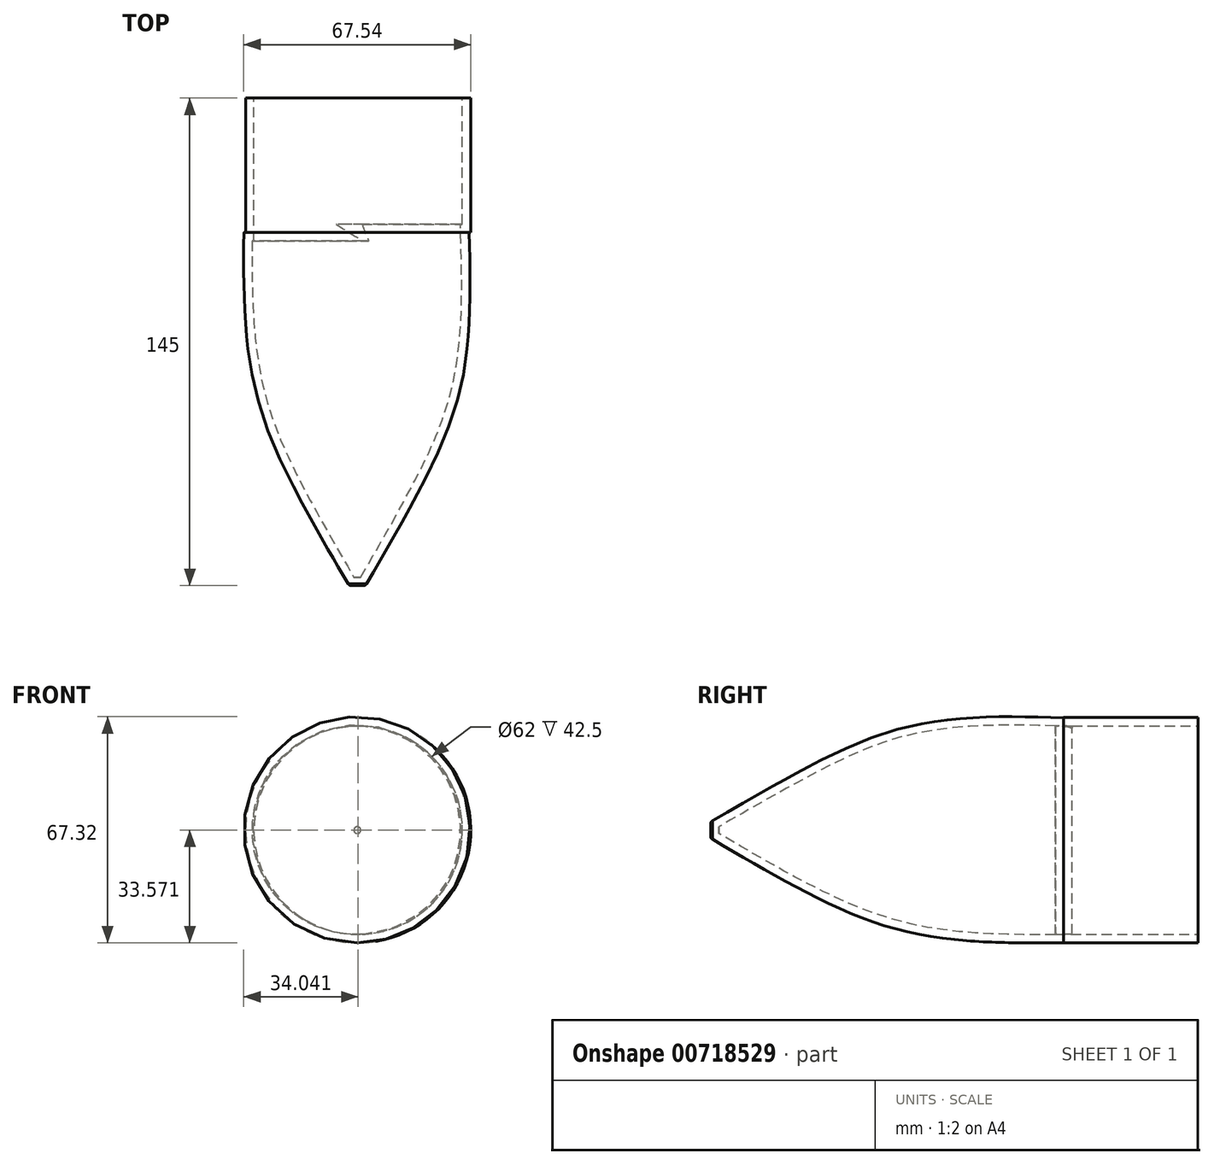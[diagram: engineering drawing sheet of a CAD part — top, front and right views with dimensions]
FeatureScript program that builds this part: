
annotation { "Feature Type Name" : "Feature", "Feature Type Description" : "" }
export const myFeature = defineFeature(function(context is Context, id is Id, definition is map)
    precondition{}
    {
        {
            var Q0;
            Q0=qCreatedBy(makeId("Front.planeOp"),FACE);
            var sketch = newSketch(context, id + "F0", { "sketchPlane" : qUnion([Q0])});
            skCircle(sketch, "E0", {"center": v(-3.3, -0.68) * mm, "radius": 32.5 * mm});
            skSolve(sketch);
        }
        {
            var Q0;
            Q0=qCreatedBy(makeId("Front.planeOp"),FACE);
            cPlane(context, id + "F1", {"entities" : qUnion([Q0]), "cplaneType" : CPlaneType.OFFSET, "offset" : 30 * mm, "width" : 150 * mm, "height" : 150 * mm});
        }
        {
            var Q0;
            Q0=qCreatedBy(id+"F1.planeOp",FACE);
            var sketch = newSketch(context, id + "F2", { "sketchPlane" : qUnion([Q0])});
            skCircle(sketch, "E1", {"center": v(-3.08, -0.92) * mm, "radius": 33.5 * mm});
            skSolve(sketch);
        }
        {
            var Q0;
            Q0=qCreatedBy(id+"F1.planeOp",FACE);
            cPlane(context, id + "F3", {"entities" : qUnion([Q0]), "cplaneType" : CPlaneType.OFFSET, "offset" : 40 * mm, "width" : 150 * mm, "height" : 150 * mm});
        }
        {
            var Q0;
            Q0=qCreatedBy(id+"F3.planeOp",FACE);
            var sketch = newSketch(context, id + "F4", { "sketchPlane" : qUnion([Q0])});
            skCircle(sketch, "E2", {"center": v(-3.59, -0.96) * mm, "radius": 33.5 * mm});
            skSolve(sketch);
        }
        {
            var Q0;
            Q0=qCreatedBy(id+"F3.planeOp",FACE);
            cPlane(context, id + "F5", {"entities" : qUnion([Q0]), "cplaneType" : CPlaneType.OFFSET, "offset" : 50 * mm, "width" : 150 * mm, "height" : 150 * mm});
        }
        {
            var Q0;
            Q0=qCreatedBy(id+"F5.planeOp",FACE);
            cPlane(context, id + "F6", {"entities" : qUnion([Q0]), "cplaneType" : CPlaneType.OFFSET, "offset" : 30 * mm, "width" : 150 * mm, "height" : 150 * mm});
        }
        {
            var Q0;
            Q0=qCreatedBy(id+"F6.planeOp",FACE);
            cPlane(context, id + "F7", {"entities" : qUnion([Q0]), "cplaneType" : CPlaneType.OFFSET, "offset" : 25 * mm, "width" : 150 * mm, "height" : 150 * mm});
        }
        {
            var Q0;
            Q0=qCreatedBy(id+"F5.planeOp",FACE);
            var sketch = newSketch(context, id + "F8", { "sketchPlane" : qUnion([Q0])});
            skCircle(sketch, "E3", {"center": v(-3.22, -0.67) * mm, "radius": 29.62 * mm});
            skSolve(sketch);
        }
        {
            var Q0;
            Q0=qCreatedBy(id+"F6.planeOp",FACE);
            var sketch = newSketch(context, id + "F9", { "sketchPlane" : qUnion([Q0])});
            skCircle(sketch, "E4", {"center": v(-3.34, -0.96) * mm, "radius": 16.66 * mm});
            skSolve(sketch);
        }
        {
            var Q0;
            Q0=sQuery(id+"F0.wireOp",EDGE,"E0");
            extrude(context, id + "F10", {"bodyType" : ToolBodyType.SURFACE, "surfaceEntities" : qUnion([Q0]), "depth" : 30 * mm, "offsetDistance" : 25 * mm});
        }
        {
            var Q0;
            Q0=makeQuery(id+"F2.imprint","IMPRINT",FACE,{"disambiguationData":[TD([[makeQuery(id+"F2.imprint","IMPRINT",EDGE,{"derivedFrom":sQuery(id+"F2.wireOp",EDGE,"E1")}),1.0]])]});
            extrude(context, id + "F11", {"entities" : qUnion([Q0]), "depth" : 40 * mm, "offsetDistance" : 25 * mm});
        }
        {
            var Q0;
            Q0=qCreatedBy(id+"F7.planeOp",FACE);
            var sketch = newSketch(context, id + "F12", { "sketchPlane" : qUnion([Q0])});
            skCircle(sketch, "E5", {"center": v(-3.32, -0.9) * mm, "radius": 2.45 * mm});
            skSolve(sketch);
        }
        {
            var Q1;
            Q1 = qSketchRegion(id + "F4", true);
            var Q2;
            Q2 = qSketchRegion(id + "F8", true);
            var Q3;
            Q3 = qSketchRegion(id + "F9", true);
            var Q4;
            Q4 = qSketchRegion(id + "F12", true);
            loft(context, id + "F13", {"operationType" : NewBodyOperationType.ADD, "sheetProfilesArray" : [{ "sheetProfileEntities" : qUnion([Q1]) }, { "sheetProfileEntities" : qUnion([Q2]) }, { "sheetProfileEntities" : qUnion([Q3]) }, { "sheetProfileEntities" : qUnion([Q4]) }]});
        }
        {
            var Q0;
            Q0=makeQuery(id+"F11.opExtrude","CAP_FACE",FACE,{"disambiguationData":[OSD([sQuery(id+"F2.wireOp",EDGE,"E1")])],"isStart":true});
            shell(context, id + "F14", {"entities" : qUnion([Q0]), "thickness" : 2.5 * mm});
        }
        {
            var Q0;
            Q0=makeQuery(id+"F13.opLoft","MID_CAP_EDGE",EDGE,{"disambiguationData":[OSD([sQuery(id+"F12.wireOp",EDGE,"E5")])],"capPos":3.0});
            fillet(context, id + "F15", {"entities" : qUnion([Q0]), "radius" : 1 * mm, "tangentPropagation" : true, "allowEdgeOverflow" : false});
        }
    });
